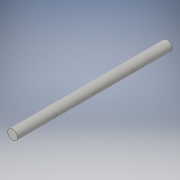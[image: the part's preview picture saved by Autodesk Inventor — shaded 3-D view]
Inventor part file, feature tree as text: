
AUTODESK INVENTOR PART (.ipt)
format: ipt  version: 2016 (Build 200138000, 138)  size: 119,808 bytes
history: native  units: in
note: dims shown in document units (in); Inventor stores cm internally (conversion verified against a paired STEP export)
features: extrude x3, sketch x2
ambient origin geometry x8: Origin, YZ Plane, XZ Plane, XY Plane, X Axis, Y Axis, Z Axis, Center Point
bodies: Solid1 (feature_tree)
feature tree (5):
  extrude  "Extrusion1"  Depth=8.0in TaperAngle=0.0deg
  extrude  "Extrusion8"  Depth=0.05in
  extrude  "Extrusion9"  Depth=2.0in
  sketch  "Sketch1"  dims[d0=0.5in d1=8.0in d2=0.0in]
  sketch  "Sketch7"  dims[d20=0.06in d21=0.05in d26=0.5in d27=0.06in d42=2.0in d43=0.1in d44=2.0in d45=0.1in d46=2.0in d47=0.1in d48=1.0in d49=0.0in d50=1.0in d51=0.0in]
